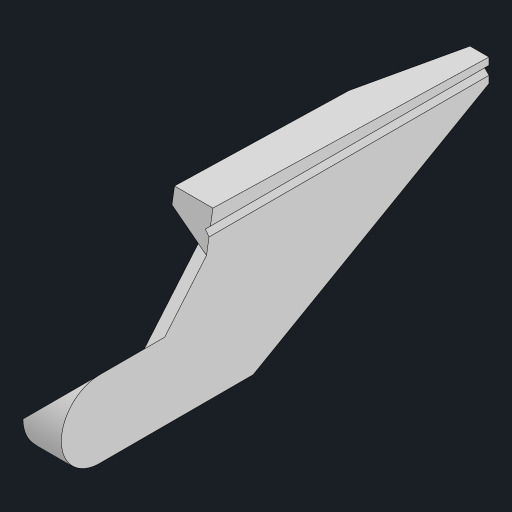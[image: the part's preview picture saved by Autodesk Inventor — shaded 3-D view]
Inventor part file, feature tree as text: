
AUTODESK INVENTOR PART (.ipt)
format: ipt  version: 2023 (Build 270158000, 158)  size: 206,336 bytes
history: native  units: mm
features: sketch x10, extrude x9, other x6, projected_geometry x2
ambient origin geometry x8: Origin, YZ Plane, XZ Plane, XY Plane, X Axis, Y Axis, Z Axis, Center Point
bodies: Body1 (feature_tree)
feature tree (27):
  other  "ソリッド1"
  extrude  "押し出し1"  Depth=0.261799mm
  other  "作業平面1"
  other  "作業平面3"
  extrude  "押し出し5"  Depth=25.0mm
  extrude  "押し出し6"  Depth=25.0mm
  sketch  "スケッチ7"
  other  "作業平面4"
  extrude  "押し出し7"  Depth=22.68928mm
  other  "作業平面5"
  extrude  "押し出し8"  Depth=1.658063mm
  extrude  "押し出し9"  Depth=60.0mm
  other  "作業平面6"
  extrude  "押し出し10"  Depth=3.0mm
  extrude  "押し出し11"  Depth=50.0mm
  extrude  "押し出し12"  Depth=100.0mm
  sketch  "スケッチ1"
  sketch  "スケッチ5"
  sketch  "スケッチ6"
  sketch  "スケッチ8"
  sketch  "スケッチ9"
  sketch  "スケッチ10"
  projected_geometry  "投影ループ1"
  projected_geometry  "投影ループ2"
  sketch  "スケッチ11"
  sketch  "スケッチ12"
  sketch  "スケッチ13"
